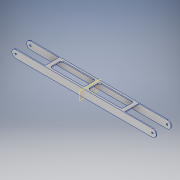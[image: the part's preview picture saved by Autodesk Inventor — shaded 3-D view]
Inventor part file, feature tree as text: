
AUTODESK INVENTOR PART (.ipt)
format: ipt  version: 2017 (Build 210142000, 142)  size: 221,184 bytes
history: native  units: in
note: dims shown in document units (in); Inventor stores cm internally (conversion verified against a paired STEP export)
features: extrude x4, sketch x4, fillet x3, projected_geometry x3, mirror x2, plane x1
ambient origin geometry x8: Origin, YZ Plane, XZ Plane, XY Plane, X Axis, Y Axis, Z Axis, Center Point
bodies: Solid1 (feature_tree)
feature tree (17):
  extrude  "Extrusion1"  Depth=1.8105in
  extrude  "Extrusion2"  Depth=0.125in
  fillet  "Fillet1"  Radius=19.0in
  extrude  "Extrusion4"  Depth=0.125in
  fillet  "Fillet2"  Radius=0.125in
  plane  "Work Plane1"
  mirror  "Mirror1"
  fillet  "Fillet3"  Radius=4.25in
  extrude  "Extrusion5"  Depth=0.125in
  mirror  "Mirror2"
  sketch  "Sketch1"  dims[d0=1.0in d2=1.8105in]
  sketch  "Sketch3"  dims[d3=0.875in d4=0.125in d5=19.0in d6=0.0in]
  projected_geometry  "Projected Loop2"
  sketch  "Sketch6"  dims[d14=2.0605in d16=4.25in d17=0.125in d18=0.0in d27=4.25in]
  projected_geometry  "Projected Loop4"
  sketch  "Sketch8"  dims[d28=1.8105in d29=0.125in d30=1.8105in d31=0.125in d32=0.125in d62=0.5in d65=10.5in d66=2.0605in d67=0.25in d68=1.5605in d69=0.5in d70=4.5in d71=1.0in d72=0.0in d73=0.25in d74=0.25in d82=0.1969in d83=0.1137in d84=30.0deg d85=150.0deg d86=30.0deg d87=150.0deg d88=0.0568in d89=0.0984in d90=3.0in d91=0.0in]
  projected_geometry  "Projected Loop6"
